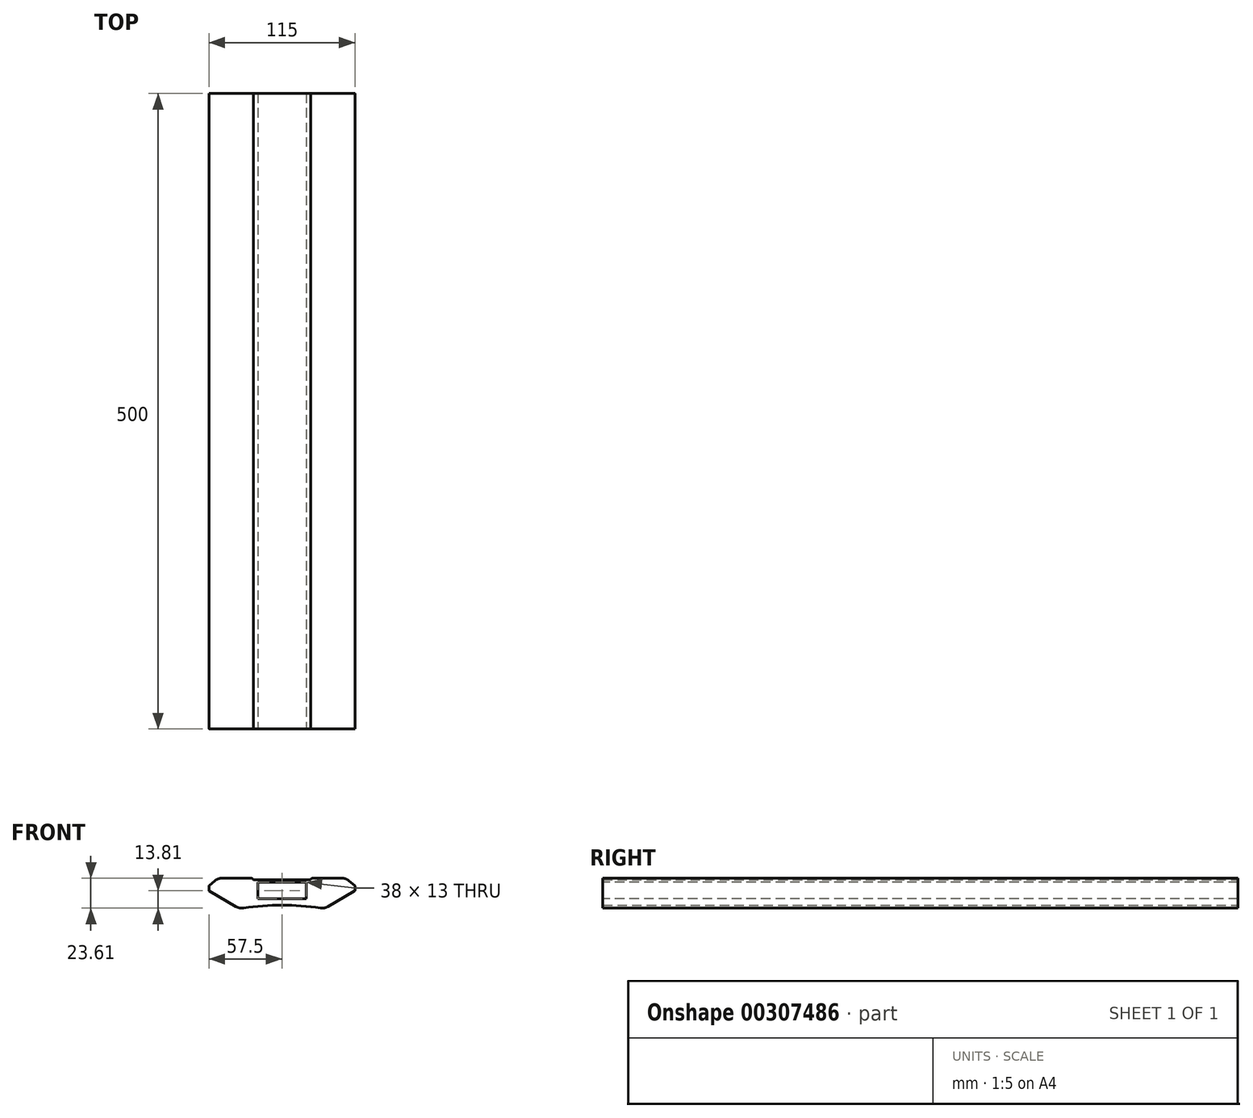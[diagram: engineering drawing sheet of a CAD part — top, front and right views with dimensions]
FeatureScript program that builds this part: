
annotation { "Feature Type Name" : "Feature", "Feature Type Description" : "" }
export const myFeature = defineFeature(function(context is Context, id is Id, definition is map)
    precondition{}
    {
        {
            var Q0;
            Q0=qCreatedBy(makeId("Front.planeOp"),FACE);
            var sketch = newSketch(context, id + "F0", { "sketchPlane" : qUnion([Q0])});
            skLineSegment(sketch, "E0", {"start": v(0, 0) * mm, "end": v(0, 15.53) * mm, "construction": true});
            skLineSegment(sketch, "E1", {"start": v(0, 0) * mm, "end": v(22.5, 0) * mm});
            skLineSegment(sketch, "E2", {"start": v(22.5, 0) * mm, "end": v(22.5, 1.3) * mm});
            skLineSegment(sketch, "E3", {"start": v(22.5, 1.3) * mm, "end": v(50.35, 1.3) * mm});
            skLineSegment(sketch, "E4", {"start": v(50.35, 1.3) * mm, "end": v(57.5, -4.7) * mm});
            skLineSegment(sketch, "E5", {"start": v(57.5, -4.7) * mm, "end": v(57.5, -8.7) * mm});
            skLineSegment(sketch, "E6", {"start": v(57.5, -8.7) * mm, "end": v(33.25, -22.7) * mm});
            skLineSegment(sketch, "E7.MirrorCS", {"start": v(0, 0) * mm, "end": v(-22.5, 0) * mm});
            skLineSegment(sketch, "E8.MirrorCS", {"start": v(-22.5, 0) * mm, "end": v(-22.5, 1.3) * mm});
            skLineSegment(sketch, "E9.MirrorCS", {"start": v(-22.5, 1.3) * mm, "end": v(-50.35, 1.3) * mm});
            skLineSegment(sketch, "E10.MirrorCS", {"start": v(-50.35, 1.3) * mm, "end": v(-57.5, -4.7) * mm});
            skLineSegment(sketch, "E11.MirrorCS", {"start": v(-57.5, -4.7) * mm, "end": v(-57.5, -8.7) * mm});
            skLineSegment(sketch, "E12.MirrorCS", {"start": v(-57.5, -8.7) * mm, "end": v(-33.25, -22.7) * mm});
            skArc(sketch, "E13", {"start": v(33.25, -22.7) * mm, "mid": v(0, -19.92) * mm, "end": v(-33.25, -22.7) * mm});
            skSolve(sketch);
        }
        {
            var Q0;
            Q0 = qSketchRegion(id + "F0", true);
            extrude(context, id + "F1", {"entities" : qUnion([Q0]), "endBound" : BoundingType.SYMMETRIC, "depth" : 500 * mm});
        }
        {
            var Q0;
            Q0=qCreatedBy(makeId("Front.planeOp"),FACE);
            var sketch = newSketch(context, id + "F2", { "sketchPlane" : qUnion([Q0])});
            skLineSegment(sketch, "E14.bottom", {"start": v(-19, -2) * mm, "end": v(19, -2) * mm});
            skLineSegment(sketch, "E14.top", {"start": v(-19, -15) * mm, "end": v(19, -15) * mm});
            skLineSegment(sketch, "E14.left", {"start": v(-19, -2) * mm, "end": v(-19, -15) * mm});
            skLineSegment(sketch, "E14.right", {"start": v(19, -2) * mm, "end": v(19, -15) * mm});
            skSolve(sketch);
        }
        {
            var Q0;
            Q0 = qSketchRegion(id + "F2", true);
            extrude(context, id + "F3", {"entities" : qUnion([Q0]), "operationType" : NewBodyOperationType.REMOVE, "endBound" : BoundingType.SYMMETRIC, "oppositeDirection" : true, "depth" : 500 * mm});
        }
        {
            var Q0;
            Q0=makeQuery(id+"F1.opExtrude","SWEPT_EDGE",EDGE,{"disambiguationData":[OSD([sQuery(id+"F0.wireOp",EDGE,"E8.MirrorCS"),sQuery(id+"F0.wireOp",EDGE,"E9.MirrorCS")])]});
            var Q1;
            Q1=makeQuery(id+"F1.opExtrude","SWEPT_EDGE",EDGE,{"disambiguationData":[OSD([sQuery(id+"F0.wireOp",EDGE,"E2"),sQuery(id+"F0.wireOp",EDGE,"E3")])]});
            fillet(context, id + "F4", {"entities" : qUnion([Q0, Q1]), "radius" : 2 * mm, "tangentPropagation" : true, "allowEdgeOverflow" : false});
        }
        {
            var Q0;
            Q0=makeQuery(id+"F1.opExtrude","SWEPT_EDGE",EDGE,{"disambiguationData":[OSD([sQuery(id+"F0.wireOp",EDGE,"E3"),sQuery(id+"F0.wireOp",EDGE,"E4")])]});
            var Q1;
            Q1=makeQuery(id+"F1.opExtrude","SWEPT_EDGE",EDGE,{"disambiguationData":[OSD([sQuery(id+"F0.wireOp",EDGE,"E6"),sQuery(id+"F0.wireOp",EDGE,"E13")])]});
            var Q2;
            Q2=makeQuery(id+"F1.opExtrude","SWEPT_EDGE",EDGE,{"disambiguationData":[OSD([sQuery(id+"F0.wireOp",EDGE,"E12.MirrorCS"),sQuery(id+"F0.wireOp",EDGE,"E13")])]});
            var Q3;
            Q3=makeQuery(id+"F1.opExtrude","SWEPT_EDGE",EDGE,{"disambiguationData":[OSD([sQuery(id+"F0.wireOp",EDGE,"E9.MirrorCS"),sQuery(id+"F0.wireOp",EDGE,"E10.MirrorCS")])]});
            fillet(context, id + "F5", {"entities" : qUnion([Q0, Q1, Q2, Q3]), "radius" : 9 * mm, "tangentPropagation" : true, "allowEdgeOverflow" : false});
        }
        {
            var Q0;
            Q0=makeQuery(id+"F1.opExtrude","SWEPT_EDGE",EDGE,{"disambiguationData":[OSD([sQuery(id+"F0.wireOp",EDGE,"E10.MirrorCS"),sQuery(id+"F0.wireOp",EDGE,"E11.MirrorCS")])]});
            var Q1;
            Q1=makeQuery(id+"F1.opExtrude","SWEPT_EDGE",EDGE,{"disambiguationData":[OSD([sQuery(id+"F0.wireOp",EDGE,"E11.MirrorCS"),sQuery(id+"F0.wireOp",EDGE,"E12.MirrorCS")])]});
            var Q2;
            Q2=makeQuery(id+"F1.opExtrude","SWEPT_EDGE",EDGE,{"disambiguationData":[OSD([sQuery(id+"F0.wireOp",EDGE,"E5"),sQuery(id+"F0.wireOp",EDGE,"E6")])]});
            var Q3;
            Q3=makeQuery(id+"F1.opExtrude","SWEPT_EDGE",EDGE,{"disambiguationData":[OSD([sQuery(id+"F0.wireOp",EDGE,"E4"),sQuery(id+"F0.wireOp",EDGE,"E5")])]});
            fillet(context, id + "F6", {"entities" : qUnion([Q0, Q1, Q2, Q3]), "radius" : 1 * mm, "tangentPropagation" : true, "allowEdgeOverflow" : false});
        }
        {
            var Q0;
            Q0=makeQuery(id+"F1.opExtrude","CAP_FACE",FACE,{"disambiguationData":[OSD([sQuery(id+"F0.wireOp",EDGE,"E1"),sQuery(id+"F0.wireOp",EDGE,"E2"),sQuery(id+"F0.wireOp",EDGE,"E3"),sQuery(id+"F0.wireOp",EDGE,"E4"),sQuery(id+"F0.wireOp",EDGE,"E5"),sQuery(id+"F0.wireOp",EDGE,"E6"),sQuery(id+"F0.wireOp",EDGE,"E7.MirrorCS"),sQuery(id+"F0.wireOp",EDGE,"E8.MirrorCS"),sQuery(id+"F0.wireOp",EDGE,"E9.MirrorCS"),sQuery(id+"F0.wireOp",EDGE,"E10.MirrorCS"),sQuery(id+"F0.wireOp",EDGE,"E11.MirrorCS"),sQuery(id+"F0.wireOp",EDGE,"E12.MirrorCS"),sQuery(id+"F0.wireOp",EDGE,"E13")])],"isStart":false});
            var sketch = newSketch(context, id + "F7", { "sketchPlane" : qUnion([Q0])});
            skLineSegment(sketch, "E15.0.0", {"start": v(36.02, -21.1) * mm, "end": v(57, -8.99) * mm});
            skArc(sketch, "E15.0.1", {"start": v(57, -8.99) * mm, "mid": v(57.37, -8.62) * mm, "end": v(57.5, -8.12) * mm});
            skLineSegment(sketch, "E15.0.2", {"start": v(57.5, -8.12) * mm, "end": v(57.5, -5.17) * mm});
            skArc(sketch, "E15.0.3", {"start": v(57.5, -5.17) * mm, "mid": v(57.4, -4.74) * mm, "end": v(57.14, -4.4) * mm});
            skLineSegment(sketch, "E15.0.4", {"start": v(57.14, -4.4) * mm, "end": v(52.86, -0.8) * mm});
            skArc(sketch, "E15.0.5", {"start": v(52.86, -0.8) * mm, "mid": v(50.15, 0.76) * mm, "end": v(47.07, 1.3) * mm});
            skLineSegment(sketch, "E15.0.6", {"start": v(47.07, 1.3) * mm, "end": v(24.37, 1.3) * mm});
            skArc(sketch, "E15.0.7", {"start": v(24.37, 1.3) * mm, "mid": v(23.23, 0.94) * mm, "end": v(22.5, 0) * mm});
            skLineSegment(sketch, "E15.0.8", {"start": v(22.5, 0) * mm, "end": v(-22.5, 0) * mm});
            skArc(sketch, "E15.0.9", {"start": v(-22.5, 0) * mm, "mid": v(-23.23, 0.94) * mm, "end": v(-24.37, 1.3) * mm});
            skLineSegment(sketch, "E15.0.10", {"start": v(-24.37, 1.3) * mm, "end": v(-47.07, 1.3) * mm});
            skArc(sketch, "E15.0.11", {"start": v(-47.07, 1.3) * mm, "mid": v(-50.15, 0.76) * mm, "end": v(-52.86, -0.8) * mm});
            skLineSegment(sketch, "E15.0.12", {"start": v(-52.86, -0.8) * mm, "end": v(-57.14, -4.4) * mm});
            skArc(sketch, "E15.0.13", {"start": v(-57.14, -4.4) * mm, "mid": v(-57.4, -4.74) * mm, "end": v(-57.5, -5.17) * mm});
            skLineSegment(sketch, "E15.0.14", {"start": v(-57.5, -5.17) * mm, "end": v(-57.5, -8.12) * mm});
            skArc(sketch, "E15.0.15", {"start": v(-57.5, -8.12) * mm, "mid": v(-57.37, -8.62) * mm, "end": v(-57, -8.99) * mm});
            skLineSegment(sketch, "E15.0.16", {"start": v(-57, -8.99) * mm, "end": v(-36.02, -21.1) * mm});
            skArc(sketch, "E15.0.17", {"start": v(-36.02, -21.1) * mm, "mid": v(-33.19, -22.15) * mm, "end": v(-30.16, -22.2) * mm});
            skArc(sketch, "E15.0.18", {"start": v(-30.16, -22.2) * mm, "mid": v(0, -19.92) * mm, "end": v(30.16, -22.2) * mm});
            skArc(sketch, "E15.0.19", {"start": v(30.16, -22.2) * mm, "mid": v(33.19, -22.15) * mm, "end": v(36.02, -21.1) * mm});
            skArc(sketch, "E16.0", {"start": v(-29.86, -24.18) * mm, "mid": v(-25.44, -23.56) * mm, "end": v(-21, -23.03) * mm});
            skArc(sketch, "E16.1", {"start": v(-42.37, -15.13) * mm, "mid": v(-37.97, -22.22) * mm, "end": v(-29.86, -24.18) * mm});
            skLineSegment(sketch, "E16.2", {"start": v(-24.37, -0.7) * mm, "end": v(-38.59, -0.7) * mm});
            skArc(sketch, "E16.3", {"start": v(-38.59, -0.7) * mm, "mid": v(-41.5, 1.78) * mm, "end": v(-45.07, 3.12) * mm});
            skLineSegment(sketch, "E16.4", {"start": v(-45.07, 3.12) * mm, "end": v(-55.76, -5.85) * mm});
            skLineSegment(sketch, "E16.5", {"start": v(-55.61, -7.48) * mm, "end": v(-42.37, -15.13) * mm});
            skPoint(sketch, "E17.visualSharp", {"position": v(-56.85, -6.77) * mm});
            skArc(sketch, "E17.filletArc", {"start": v(-55.76, -5.85) * mm, "mid": v(-56.1, -6.7) * mm, "end": v(-55.61, -7.48) * mm});
            skLineSegment(sketch, "E18", {"start": v(-21, -23.03) * mm, "end": v(-21, -2) * mm});
            skLineSegment(sketch, "E19", {"start": v(-21, -2) * mm, "end": v(-22.5, -2) * mm});
            skArc(sketch, "E20", {"start": v(-22.5, -2) * mm, "mid": v(-23.23, -1.06) * mm, "end": v(-24.37, -0.7) * mm});
            skLineSegment(sketch, "E21.MirrorCS", {"start": v(21, -23.03) * mm, "end": v(21, -2) * mm});
            skLineSegment(sketch, "E22.MirrorCS", {"start": v(21, -2) * mm, "end": v(22.5, -2) * mm});
            skArc(sketch, "E23.MirrorCS", {"start": v(22.5, -2) * mm, "mid": v(23.23, -1.06) * mm, "end": v(24.37, -0.7) * mm});
            skLineSegment(sketch, "E24.MirrorCS", {"start": v(24.37, -0.7) * mm, "end": v(38.59, -0.7) * mm});
            skArc(sketch, "E25.MirrorCS", {"start": v(29.86, -24.18) * mm, "mid": v(25.44, -23.56) * mm, "end": v(21, -23.03) * mm});
            skArc(sketch, "E26.MirrorCS", {"start": v(42.37, -15.13) * mm, "mid": v(37.97, -22.22) * mm, "end": v(29.86, -24.18) * mm});
            skLineSegment(sketch, "E27.MirrorCS", {"start": v(55.61, -7.48) * mm, "end": v(42.37, -15.13) * mm});
            skArc(sketch, "E28.MirrorCS", {"start": v(38.59, -0.7) * mm, "mid": v(41.5, 1.78) * mm, "end": v(45.07, 3.12) * mm});
            skLineSegment(sketch, "E29.MirrorCS", {"start": v(45.07, 3.12) * mm, "end": v(55.76, -5.85) * mm});
            skArc(sketch, "E30.MirrorCS", {"start": v(55.76, -5.85) * mm, "mid": v(56.1, -6.7) * mm, "end": v(55.61, -7.48) * mm});
            skArc(sketch, "E31.trimOffspring", {"start": v(-21, -23.03) * mm, "mid": v(-25.44, -23.56) * mm, "end": v(-29.86, -24.18) * mm});
            skArc(sketch, "E32.trimOffspring", {"start": v(21, -23.03) * mm, "mid": v(25.44, -23.56) * mm, "end": v(29.86, -24.18) * mm});
            skSolve(sketch);
        }
        {
            var Q0;
            Q0=makeQuery(id+"F7.imprint","IMPRINT",FACE,{"disambiguationData":[TD([[makeQuery(id+"F7.imprint","IMPRINT",EDGE,{"derivedFrom":sQuery(id+"F7.wireOp",EDGE,"E21.MirrorCS")}),-1.0]])]});
            var Q1;
            Q1=makeQuery(id+"F7.imprint","IMPRINT",FACE,{"disambiguationData":[TD([[makeQuery(id+"F7.imprint","IMPRINT",EDGE,{"derivedFrom":sQuery(id+"F7.wireOp",EDGE,"E16.1")}),1.0]])]});
            extrude(context, id + "F8", {"entities" : qUnion([Q0, Q1]), "operationType" : NewBodyOperationType.REMOVE, "endBound" : BoundingType.THROUGH_ALL, "oppositeDirection" : true, "depth" : 25 * mm});
        }
    });
